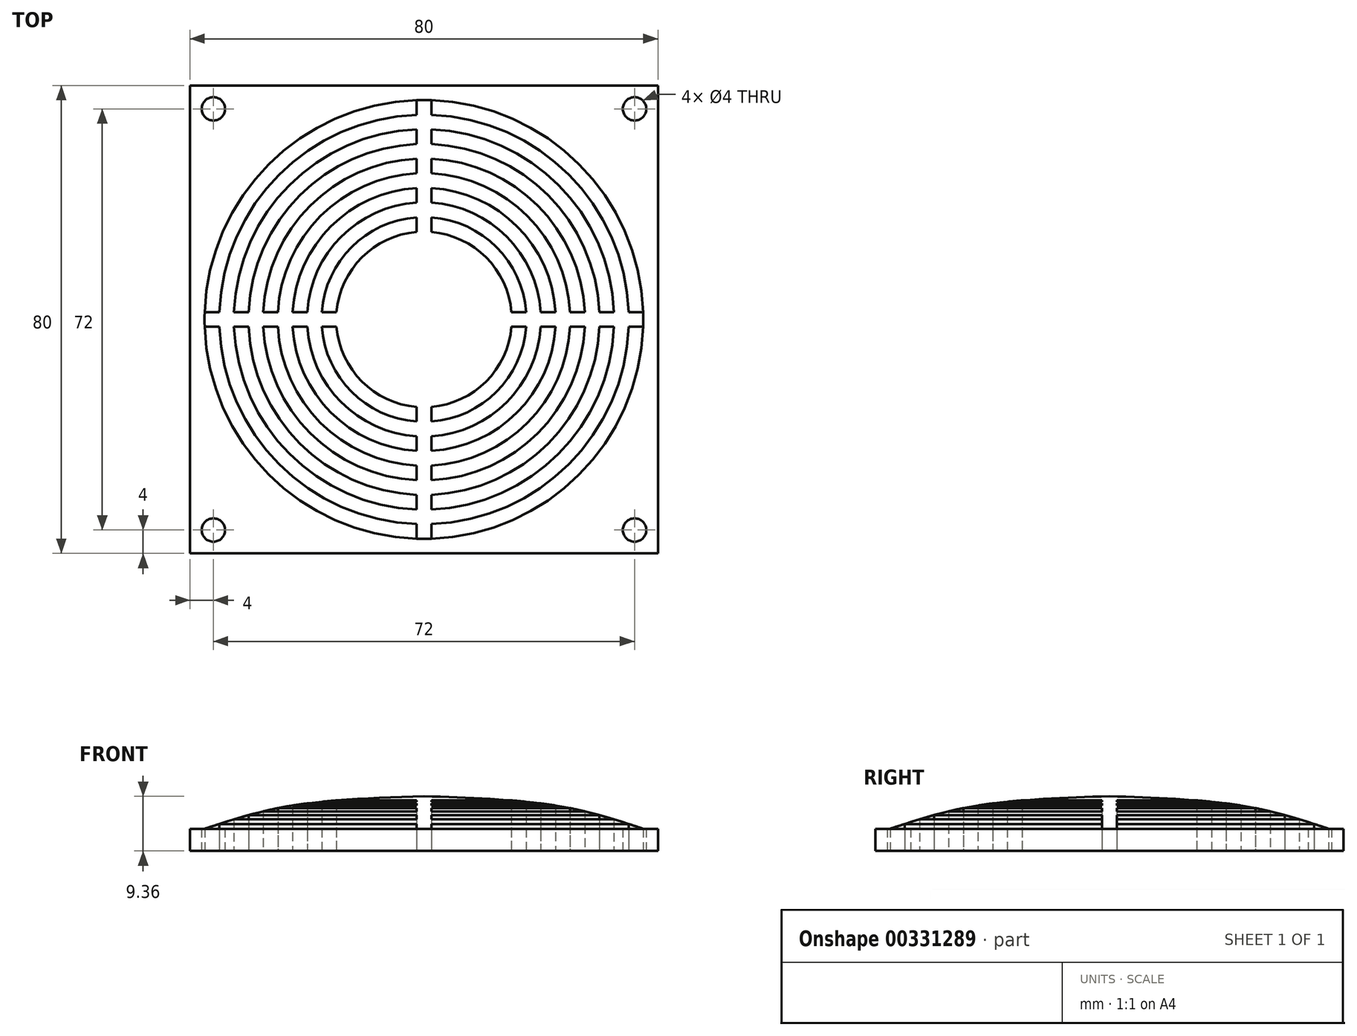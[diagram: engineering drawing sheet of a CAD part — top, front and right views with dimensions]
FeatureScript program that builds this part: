
annotation { "Feature Type Name" : "Feature", "Feature Type Description" : "" }
export const myFeature = defineFeature(function(context is Context, id is Id, definition is map)
    precondition{}
    {
        {
            var Q0;
            Q0=qCreatedBy(makeId("Top.planeOp"),FACE);
            var sketch = newSketch(context, id + "F0", { "sketchPlane" : qUnion([Q0])});
            skPoint(sketch, "E0.middle", {"position": v(0, 0) * mm});
            skCircle(sketch, "E1", {"center": v(0, 0) * mm, "radius": 37.5 * mm});
            skCircle(sketch, "E2", {"center": v(36, 36) * mm, "radius": 2 * mm});
            skCircle(sketch, "E3", {"center": v(-36, 36) * mm, "radius": 2 * mm});
            skCircle(sketch, "E4", {"center": v(-36, -36) * mm, "radius": 2 * mm});
            skCircle(sketch, "E5", {"center": v(36, -36) * mm, "radius": 2 * mm});
            skLineSegment(sketch, "E6.bottom", {"start": v(40, 40) * mm, "end": v(-40, 40) * mm});
            skLineSegment(sketch, "E6.top", {"start": v(40, -40) * mm, "end": v(-40, -40) * mm});
            skLineSegment(sketch, "E6.left", {"start": v(40, 40) * mm, "end": v(40, -40) * mm});
            skLineSegment(sketch, "E6.right", {"start": v(-40, 40) * mm, "end": v(-40, -40) * mm});
            skCircle(sketch, "E7", {"center": v(0, 0) * mm, "radius": 15 * mm});
            skLineSegment(sketch, "E8.bottom", {"start": v(-1.25, 40) * mm, "end": v(1.25, 40) * mm});
            skLineSegment(sketch, "E8.top", {"start": v(-1.25, -40) * mm, "end": v(1.25, -40) * mm});
            skLineSegment(sketch, "E8.left", {"start": v(-1.25, 37.48) * mm, "end": v(-1.25, 34.98) * mm});
            skLineSegment(sketch, "E8.right", {"start": v(1.25, 37.48) * mm, "end": v(1.25, 34.98) * mm});
            skLineSegment(sketch, "E9.bottom", {"start": v(-37.48, 1.25) * mm, "end": v(-34.98, 1.25) * mm});
            skLineSegment(sketch, "E9.left", {"start": v(-40, 1.25) * mm, "end": v(-40, -1.25) * mm});
            skLineSegment(sketch, "E9.right", {"start": v(40, 1.25) * mm, "end": v(40, -1.25) * mm});
            skCircle(sketch, "E10", {"center": v(0, 0) * mm, "radius": 35 * mm});
            skCircle(sketch, "E11", {"center": v(0, 0) * mm, "radius": 32.5 * mm});
            skCircle(sketch, "E12", {"center": v(0, 0) * mm, "radius": 30 * mm});
            skCircle(sketch, "E13", {"center": v(0, 0) * mm, "radius": 27.5 * mm});
            skCircle(sketch, "E14", {"center": v(0, 0) * mm, "radius": 25 * mm});
            skCircle(sketch, "E15", {"center": v(0, 0) * mm, "radius": 20 * mm});
            skCircle(sketch, "E16", {"center": v(0, 0) * mm, "radius": 22.5 * mm});
            skCircle(sketch, "E17", {"center": v(0, 0) * mm, "radius": 17.5 * mm});
            skLineSegment(sketch, "E18.trimOffspring", {"start": v(-1.25, 17.46) * mm, "end": v(-1.25, 14.95) * mm});
            skLineSegment(sketch, "E19.trimOffspring", {"start": v(1.25, 17.46) * mm, "end": v(1.25, 14.95) * mm});
            skLineSegment(sketch, "E20.trimOffspring", {"start": v(1.25, 22.47) * mm, "end": v(1.25, 19.96) * mm});
            skLineSegment(sketch, "E21.trimOffspring", {"start": v(-1.25, 22.47) * mm, "end": v(-1.25, 19.96) * mm});
            skLineSegment(sketch, "E22.trimOffspring", {"start": v(-1.25, 27.47) * mm, "end": v(-1.25, 24.97) * mm});
            skLineSegment(sketch, "E23.trimOffspring", {"start": v(1.25, 27.47) * mm, "end": v(1.25, 24.97) * mm});
            skLineSegment(sketch, "E24.trimOffspring", {"start": v(1.25, 32.48) * mm, "end": v(1.25, 29.97) * mm});
            skLineSegment(sketch, "E25.trimOffspring", {"start": v(-1.25, 32.48) * mm, "end": v(-1.25, 29.97) * mm});
            skLineSegment(sketch, "E26.trimOffspring", {"start": v(19.96, 1.25) * mm, "end": v(22.47, 1.25) * mm});
            skLineSegment(sketch, "E27.trimOffspring", {"start": v(19.96, -1.25) * mm, "end": v(22.47, -1.25) * mm});
            skLineSegment(sketch, "E28.trimOffspring", {"start": v(24.97, 1.25) * mm, "end": v(27.47, 1.25) * mm});
            skLineSegment(sketch, "E29.trimOffspring", {"start": v(24.97, -1.25) * mm, "end": v(27.47, -1.25) * mm});
            skLineSegment(sketch, "E30.trimOffspring", {"start": v(29.97, 1.25) * mm, "end": v(32.48, 1.25) * mm});
            skLineSegment(sketch, "E31.trimOffspring", {"start": v(29.97, -1.25) * mm, "end": v(32.48, -1.25) * mm});
            skLineSegment(sketch, "E32.trimOffspring", {"start": v(34.98, -1.25) * mm, "end": v(37.48, -1.25) * mm});
            skLineSegment(sketch, "E33.trimOffspring", {"start": v(34.98, 1.25) * mm, "end": v(37.48, 1.25) * mm});
            skLineSegment(sketch, "E34.trimOffspring", {"start": v(-1.25, -19.96) * mm, "end": v(-1.25, -22.47) * mm});
            skLineSegment(sketch, "E35.trimOffspring", {"start": v(1.25, -19.96) * mm, "end": v(1.25, -22.47) * mm});
            skLineSegment(sketch, "E36.trimOffspring", {"start": v(1.25, -24.97) * mm, "end": v(1.25, -27.47) * mm});
            skLineSegment(sketch, "E37.trimOffspring", {"start": v(1.25, -29.97) * mm, "end": v(1.25, -32.48) * mm});
            skLineSegment(sketch, "E38.trimOffspring", {"start": v(1.25, -34.98) * mm, "end": v(1.25, -37.48) * mm});
            skLineSegment(sketch, "E39.trimOffspring", {"start": v(-1.25, -34.98) * mm, "end": v(-1.25, -37.48) * mm});
            skLineSegment(sketch, "E40.trimOffspring", {"start": v(-1.25, -29.97) * mm, "end": v(-1.25, -32.48) * mm});
            skLineSegment(sketch, "E41.trimOffspring", {"start": v(-1.25, -24.97) * mm, "end": v(-1.25, -27.47) * mm});
            skLineSegment(sketch, "E42.trimOffspring", {"start": v(-17.46, 1.25) * mm, "end": v(-14.95, 1.25) * mm});
            skLineSegment(sketch, "E43.trimOffspring", {"start": v(-22.47, 1.25) * mm, "end": v(-19.96, 1.25) * mm});
            skLineSegment(sketch, "E44.trimOffspring", {"start": v(-27.47, 1.25) * mm, "end": v(-24.97, 1.25) * mm});
            skLineSegment(sketch, "E45.trimOffspring", {"start": v(-32.48, 1.25) * mm, "end": v(-29.97, 1.25) * mm});
            skLineSegment(sketch, "E46.trimOffspring", {"start": v(-32.48, -1.25) * mm, "end": v(-29.97, -1.25) * mm});
            skLineSegment(sketch, "E47.trimOffspring", {"start": v(-27.47, -1.25) * mm, "end": v(-24.97, -1.25) * mm});
            skLineSegment(sketch, "E48.trimOffspring", {"start": v(-22.47, -1.25) * mm, "end": v(-19.96, -1.25) * mm});
            skLineSegment(sketch, "E49.trimOffspring", {"start": v(-17.46, -1.25) * mm, "end": v(-14.95, -1.25) * mm});
            skLineSegment(sketch, "E50.trimOffspring", {"start": v(14.95, -1.25) * mm, "end": v(17.46, -1.25) * mm});
            skLineSegment(sketch, "E51.trimOffspring", {"start": v(14.95, 1.25) * mm, "end": v(17.46, 1.25) * mm});
            skLineSegment(sketch, "E52.trimOffspring", {"start": v(1.25, -14.95) * mm, "end": v(1.25, -17.46) * mm});
            skLineSegment(sketch, "E53.trimOffspring", {"start": v(-1.25, -14.95) * mm, "end": v(-1.25, -17.46) * mm});
            skLineSegment(sketch, "E54", {"start": v(-37.48, -1.25) * mm, "end": v(-34.98, -1.25) * mm});
            skSolve(sketch);
        }
        {
            var Q0;
            Q0 = qSketchRegion(id + "F0", true);
            var Q1;
            {var subQ4=sQuery(id+"F0.wireOp",EDGE,"E10");var subQ10=makeQuery(id+"F0.imprint","INTERSECT",VERTEX,{"derivedFrom":[sQuery(id+"F0.wireOp",EDGE,"E8.right"),subQ4]});Q1=makeQuery(id+"F0.imprint","IMPRINT",FACE,{"disambiguationData":[TD([[makeQuery(id+"F0.imprint","IMPRINT",EDGE,{"disambiguationData":[TD([[subQ10,1.0]])],"derivedFrom":subQ4}),1.0]])]});}
            var Q2;
            {var subQ0=sQuery(id+"F0.wireOp",EDGE,"E9.bottom");Q2=makeQuery(id+"F0.imprint","IMPRINT",FACE,{"disambiguationData":[TD([[makeQuery(id+"F0.imprint","IMPRINT",EDGE,{"derivedFrom":subQ0}),-1.0]])]});}
            var Q3;
            {var subQ0=sQuery(id+"F0.wireOp",EDGE,"E45.trimOffspring");Q3=makeQuery(id+"F0.imprint","IMPRINT",FACE,{"disambiguationData":[TD([[makeQuery(id+"F0.imprint","IMPRINT",EDGE,{"derivedFrom":subQ0}),-1.0]])]});}
            var Q4;
            {var subQ4=sQuery(id+"F0.wireOp",EDGE,"E12");var subQ10=makeQuery(id+"F0.imprint","INTERSECT",VERTEX,{"derivedFrom":[subQ4,sQuery(id+"F0.wireOp",EDGE,"E24.trimOffspring")]});Q4=makeQuery(id+"F0.imprint","IMPRINT",FACE,{"disambiguationData":[TD([[makeQuery(id+"F0.imprint","IMPRINT",EDGE,{"disambiguationData":[TD([[subQ10,1.0]])],"derivedFrom":subQ4}),1.0]])]});}
            var Q5;
            {var subQ0=sQuery(id+"F0.wireOp",EDGE,"E44.trimOffspring");Q5=makeQuery(id+"F0.imprint","IMPRINT",FACE,{"disambiguationData":[TD([[makeQuery(id+"F0.imprint","IMPRINT",EDGE,{"derivedFrom":subQ0}),-1.0]])]});}
            var Q6;
            {var subQ0=sQuery(id+"F0.wireOp",EDGE,"E14");var subQ10=makeQuery(id+"F0.imprint","INTERSECT",VERTEX,{"derivedFrom":[subQ0,sQuery(id+"F0.wireOp",EDGE,"E23.trimOffspring")]});Q6=makeQuery(id+"F0.imprint","IMPRINT",FACE,{"disambiguationData":[TD([[makeQuery(id+"F0.imprint","IMPRINT",EDGE,{"disambiguationData":[TD([[subQ10,1.0]])],"derivedFrom":subQ0}),1.0]])]});}
            var Q7;
            {var subQ0=sQuery(id+"F0.wireOp",EDGE,"E43.trimOffspring");Q7=makeQuery(id+"F0.imprint","IMPRINT",FACE,{"disambiguationData":[TD([[makeQuery(id+"F0.imprint","IMPRINT",EDGE,{"derivedFrom":subQ0}),-1.0]])]});}
            var Q8;
            {var subQ0=sQuery(id+"F0.wireOp",EDGE,"E15");var subQ10=makeQuery(id+"F0.imprint","INTERSECT",VERTEX,{"derivedFrom":[subQ0,sQuery(id+"F0.wireOp",EDGE,"E20.trimOffspring")]});Q8=makeQuery(id+"F0.imprint","IMPRINT",FACE,{"disambiguationData":[TD([[makeQuery(id+"F0.imprint","IMPRINT",EDGE,{"disambiguationData":[TD([[subQ10,1.0]])],"derivedFrom":subQ0}),1.0]])]});}
            var Q9;
            {var subQ0=sQuery(id+"F0.wireOp",EDGE,"E42.trimOffspring");Q9=makeQuery(id+"F0.imprint","IMPRINT",FACE,{"disambiguationData":[TD([[makeQuery(id+"F0.imprint","IMPRINT",EDGE,{"derivedFrom":subQ0}),-1.0]])]});}
            var Q10;
            {var subQ0=sQuery(id+"F0.wireOp",EDGE,"E7");var subQ4=makeQuery(id+"F0.imprint","INTERSECT",VERTEX,{"derivedFrom":[subQ0,sQuery(id+"F0.wireOp",EDGE,"E19.trimOffspring")]});Q10=makeQuery(id+"F0.imprint","IMPRINT",FACE,{"disambiguationData":[TD([[makeQuery(id+"F0.imprint","IMPRINT",EDGE,{"disambiguationData":[TD([[subQ4,1.0]])],"derivedFrom":subQ0}),1.0]])]});}
            var Q11;
            {var subQ0=sQuery(id+"F0.wireOp",EDGE,"E50.trimOffspring");Q11=makeQuery(id+"F0.imprint","IMPRINT",FACE,{"disambiguationData":[TD([[makeQuery(id+"F0.imprint","IMPRINT",EDGE,{"derivedFrom":subQ0}),1.0]])]});}
            var Q12;
            {var subQ0=sQuery(id+"F0.wireOp",EDGE,"E26.trimOffspring");Q12=makeQuery(id+"F0.imprint","IMPRINT",FACE,{"disambiguationData":[TD([[makeQuery(id+"F0.imprint","IMPRINT",EDGE,{"derivedFrom":subQ0}),-1.0]])]});}
            var Q13;
            {var subQ0=sQuery(id+"F0.wireOp",EDGE,"E28.trimOffspring");Q13=makeQuery(id+"F0.imprint","IMPRINT",FACE,{"disambiguationData":[TD([[makeQuery(id+"F0.imprint","IMPRINT",EDGE,{"derivedFrom":subQ0}),-1.0]])]});}
            var Q14;
            {var subQ0=sQuery(id+"F0.wireOp",EDGE,"E30.trimOffspring");Q14=makeQuery(id+"F0.imprint","IMPRINT",FACE,{"disambiguationData":[TD([[makeQuery(id+"F0.imprint","IMPRINT",EDGE,{"derivedFrom":subQ0}),-1.0]])]});}
            var Q15;
            {var subQ0=sQuery(id+"F0.wireOp",EDGE,"E32.trimOffspring");Q15=makeQuery(id+"F0.imprint","IMPRINT",FACE,{"disambiguationData":[TD([[makeQuery(id+"F0.imprint","IMPRINT",EDGE,{"derivedFrom":subQ0}),1.0]])]});}
            var Q16;
            {var subQ0=sQuery(id+"F0.wireOp",EDGE,"E18.trimOffspring");Q16=makeQuery(id+"F0.imprint","IMPRINT",FACE,{"disambiguationData":[TD([[makeQuery(id+"F0.imprint","IMPRINT",EDGE,{"derivedFrom":subQ0}),1.0]])]});}
            var Q17;
            {var subQ0=sQuery(id+"F0.wireOp",EDGE,"E20.trimOffspring");Q17=makeQuery(id+"F0.imprint","IMPRINT",FACE,{"disambiguationData":[TD([[makeQuery(id+"F0.imprint","IMPRINT",EDGE,{"derivedFrom":subQ0}),-1.0]])]});}
            var Q18;
            {var subQ0=sQuery(id+"F0.wireOp",EDGE,"E22.trimOffspring");Q18=makeQuery(id+"F0.imprint","IMPRINT",FACE,{"disambiguationData":[TD([[makeQuery(id+"F0.imprint","IMPRINT",EDGE,{"derivedFrom":subQ0}),1.0]])]});}
            var Q19;
            {var subQ0=sQuery(id+"F0.wireOp",EDGE,"E24.trimOffspring");Q19=makeQuery(id+"F0.imprint","IMPRINT",FACE,{"disambiguationData":[TD([[makeQuery(id+"F0.imprint","IMPRINT",EDGE,{"derivedFrom":subQ0}),-1.0]])]});}
            var Q20;
            {var subQ0=sQuery(id+"F0.wireOp",EDGE,"E8.left");Q20=makeQuery(id+"F0.imprint","IMPRINT",FACE,{"disambiguationData":[TD([[makeQuery(id+"F0.imprint","IMPRINT",EDGE,{"derivedFrom":subQ0}),1.0]])]});}
            var Q21;
            {var subQ0=sQuery(id+"F0.wireOp",EDGE,"E52.trimOffspring");Q21=makeQuery(id+"F0.imprint","IMPRINT",FACE,{"disambiguationData":[TD([[makeQuery(id+"F0.imprint","IMPRINT",EDGE,{"derivedFrom":subQ0}),-1.0]])]});}
            var Q22;
            {var subQ0=sQuery(id+"F0.wireOp",EDGE,"E34.trimOffspring");Q22=makeQuery(id+"F0.imprint","IMPRINT",FACE,{"disambiguationData":[TD([[makeQuery(id+"F0.imprint","IMPRINT",EDGE,{"derivedFrom":subQ0}),1.0]])]});}
            var Q23;
            {var subQ0=sQuery(id+"F0.wireOp",EDGE,"E36.trimOffspring");Q23=makeQuery(id+"F0.imprint","IMPRINT",FACE,{"disambiguationData":[TD([[makeQuery(id+"F0.imprint","IMPRINT",EDGE,{"derivedFrom":subQ0}),-1.0]])]});}
            var Q24;
            {var subQ0=sQuery(id+"F0.wireOp",EDGE,"E37.trimOffspring");Q24=makeQuery(id+"F0.imprint","IMPRINT",FACE,{"disambiguationData":[TD([[makeQuery(id+"F0.imprint","IMPRINT",EDGE,{"derivedFrom":subQ0}),-1.0]])]});}
            var Q25;
            {var subQ0=sQuery(id+"F0.wireOp",EDGE,"E38.trimOffspring");Q25=makeQuery(id+"F0.imprint","IMPRINT",FACE,{"disambiguationData":[TD([[makeQuery(id+"F0.imprint","IMPRINT",EDGE,{"derivedFrom":subQ0}),-1.0]])]});}
            extrude(context, id + "F1", {"entities" : qUnion([Q0, Q1, Q2, Q3, Q4, Q5, Q6, Q7, Q8, Q9, Q10, Q11, Q12, Q13, Q14, Q15, Q16, Q17, Q18, Q19, Q20, Q21, Q22, Q23, Q24, Q25]), "depth" : 25 * mm});
        }
        {
            var Q0;
            Q0=qCreatedBy(makeId("Front.planeOp"),FACE);
            var sketch = newSketch(context, id + "F2", { "sketchPlane" : qUnion([Q0])});
            skFitSpline(sketch, "E55", {"points": [v(-37.5, 3.8) * mm, v(-23.05, 7.68) * mm, v(0, 9.36) * mm], "startDerivative": vector(30.36, 9.97) * mm, "endDerivative": vector(44.14, 1.46) * mm});
            skPoint(sketch, "E56.end.orphan", {"position": v(0, 17.42) * mm});
            skLineSegment(sketch, "E57", {"start": v(-37.5, 3.8) * mm, "end": v(-70.62, 3.8) * mm});
            skLineSegment(sketch, "E58", {"start": v(-70.62, 3.8) * mm, "end": v(-70.62, 49.16) * mm});
            skLineSegment(sketch, "E59", {"start": v(-70.62, 49.16) * mm, "end": v(0, 49.16) * mm});
            skLineSegment(sketch, "E60", {"start": v(0, 49.16) * mm, "end": v(0, 9.36) * mm});
            skSolve(sketch);
        }
        {
            var Q0;
            Q0=qCreatedBy(makeId("Front.planeOp"),FACE);
            var sketch = newSketch(context, id + "F3", { "sketchPlane" : qUnion([Q0])});
            skLineSegment(sketch, "E61", {"start": v(0, 0) * mm, "end": v(0, 20.47) * mm});
            skSolve(sketch);
        }
        {
            var Q0;
            Q0 = qSketchRegion(id + "F2", true);
            var Q1;
            Q1=sQuery(id+"F3.wireOp",EDGE,"E61");
            revolve(context, id + "F4", {"operationType" : NewBodyOperationType.REMOVE, "entities" : qUnion([Q0]), "axis" : qUnion([Q1]), "revolveType" : RevolveType.FULL, "oppositeDirection" : true});
        }
    });
